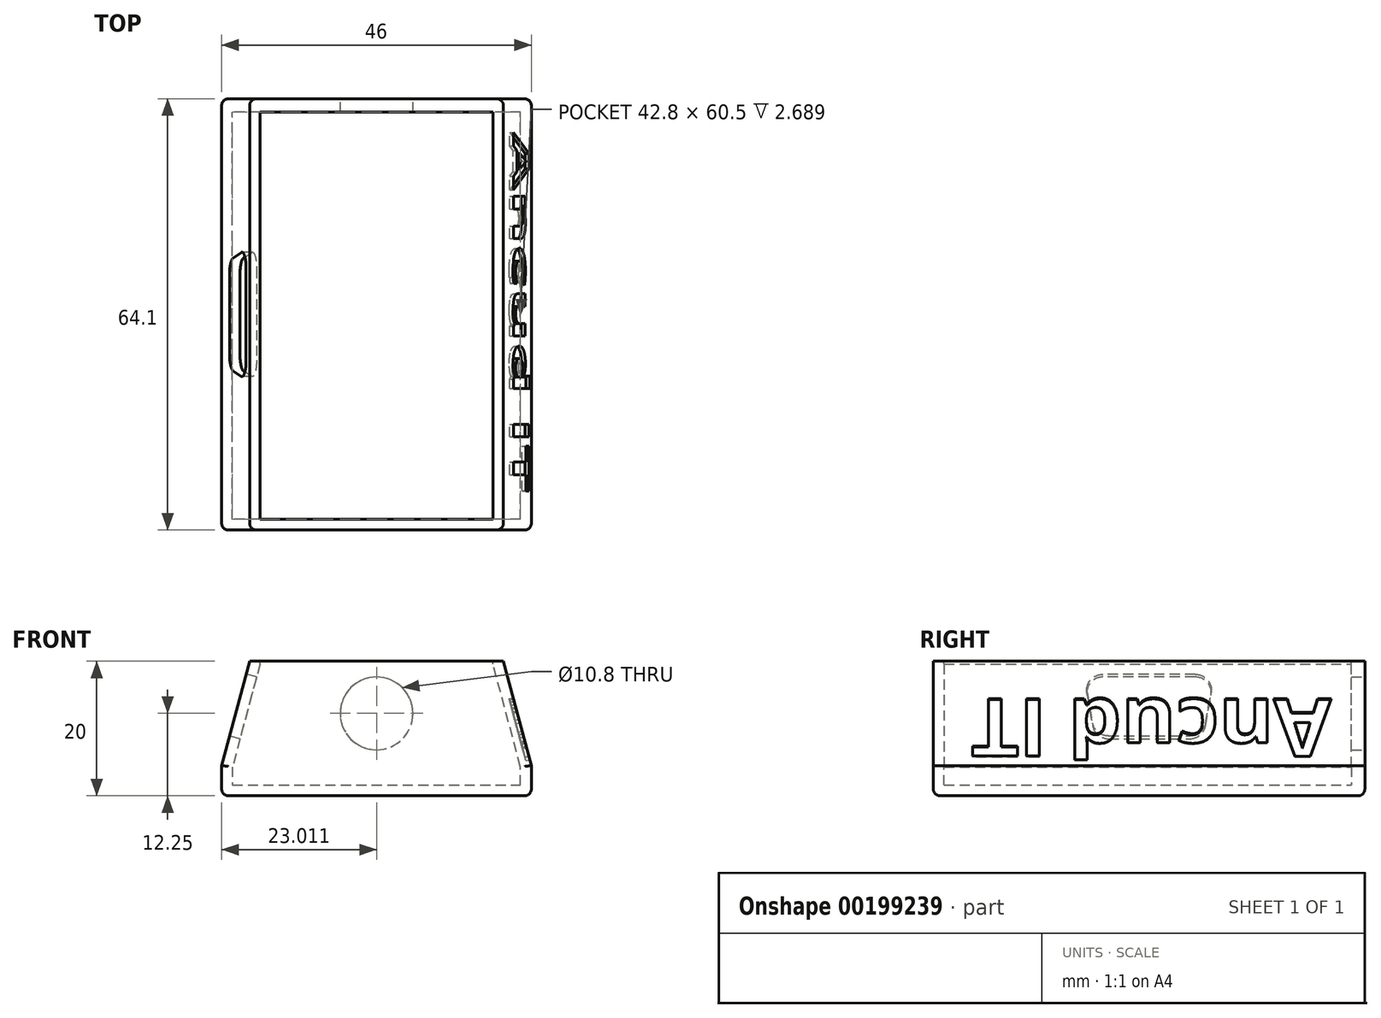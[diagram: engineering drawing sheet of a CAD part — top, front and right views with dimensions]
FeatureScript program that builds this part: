
annotation { "Feature Type Name" : "Feature", "Feature Type Description" : "" }
export const myFeature = defineFeature(function(context is Context, id is Id, definition is map)
    precondition{}
    {
        {
            var Q0;
            Q0=qCreatedBy(makeId("Front.planeOp"),FACE);
            var sketch = newSketch(context, id + "F0", { "sketchPlane" : qUnion([Q0])});
            skLineSegment(sketch, "E0", {"start": v(23, 0) * mm, "end": v(-23, 0) * mm});
            skLineSegment(sketch, "E1", {"start": v(-23, 0) * mm, "end": v(-23, 4.5) * mm});
            skLineSegment(sketch, "E2", {"start": v(-23, 4.5) * mm, "end": v(-18.85, 20) * mm});
            skLineSegment(sketch, "E3", {"start": v(-18.85, 20) * mm, "end": v(18.85, 20) * mm});
            skLineSegment(sketch, "E4", {"start": v(18.85, 20) * mm, "end": v(23, 4.5) * mm});
            skLineSegment(sketch, "E5", {"start": v(23, 4.5) * mm, "end": v(23, 0) * mm});
            skSolve(sketch);
        }
        {
            var Q0;
            Q0 = qSketchRegion(id + "F0", true);
            extrude(context, id + "F1", {"entities" : qUnion([Q0]), "depth" : 2 * mm});
        }
        {
            var Q0;
            Q0=makeQuery(id+"F1.opExtrude","CAP_FACE",FACE,{"disambiguationData":[OSD([sQuery(id+"F0.wireOp",EDGE,"E0"),sQuery(id+"F0.wireOp",EDGE,"E1"),sQuery(id+"F0.wireOp",EDGE,"E2"),sQuery(id+"F0.wireOp",EDGE,"E3"),sQuery(id+"F0.wireOp",EDGE,"E4"),sQuery(id+"F0.wireOp",EDGE,"E5")])],"isStart":false});
            var sketch = newSketch(context, id + "F2", { "sketchPlane" : qUnion([Q0])});
            skLineSegment(sketch, "E6", {"start": v(-23, 0) * mm, "end": v(23, 0) * mm});
            skLineSegment(sketch, "E7", {"start": v(23, 0) * mm, "end": v(23, 4.5) * mm});
            skLineSegment(sketch, "E8", {"start": v(23, 4.5) * mm, "end": v(18.85, 20) * mm});
            skLineSegment(sketch, "E9", {"start": v(-18.85, 20) * mm, "end": v(-23, 4.5) * mm});
            skLineSegment(sketch, "E10", {"start": v(-23, 4.5) * mm, "end": v(-23, 0) * mm});
            skLineSegment(sketch, "E11.0", {"start": v(21.4, 4.29) * mm, "end": v(17.3, 19.59) * mm});
            skLineSegment(sketch, "E11.1", {"start": v(-17.3, 19.59) * mm, "end": v(-21.4, 4.29) * mm});
            skLineSegment(sketch, "E11.2", {"start": v(-21.4, 4.29) * mm, "end": v(-21.4, 1.6) * mm});
            skLineSegment(sketch, "E11.3", {"start": v(-21.4, 1.6) * mm, "end": v(21.4, 1.6) * mm});
            skLineSegment(sketch, "E11.4", {"start": v(21.4, 1.6) * mm, "end": v(21.4, 4.29) * mm});
            skLineSegment(sketch, "E12", {"start": v(-17.3, 19.59) * mm, "end": v(-17.3, 20) * mm});
            skLineSegment(sketch, "E13", {"start": v(17.3, 19.59) * mm, "end": v(17.3, 20) * mm});
            skLineSegment(sketch, "E14", {"start": v(-18.85, 20) * mm, "end": v(-17.3, 20) * mm});
            skLineSegment(sketch, "E15", {"start": v(17.3, 20) * mm, "end": v(18.85, 20) * mm});
            skSolve(sketch);
        }
        {
            var Q0;
            Q0 = qSketchRegion(id + "F2", true);
            extrude(context, id + "F3", {"entities" : qUnion([Q0]), "operationType" : NewBodyOperationType.ADD, "depth" : 60.5 * mm});
        }
        {
            var Q0;
            Q0=makeQuery(id+"F3.opExtrude","CAP_FACE",FACE,{"disambiguationData":[OSD([sQuery(id+"F2.wireOp",EDGE,"E6"),sQuery(id+"F2.wireOp",EDGE,"E7"),sQuery(id+"F2.wireOp",EDGE,"E8"),sQuery(id+"F2.wireOp",EDGE,"E9"),sQuery(id+"F2.wireOp",EDGE,"E10"),sQuery(id+"F2.wireOp",EDGE,"E11.0"),sQuery(id+"F2.wireOp",EDGE,"E11.1"),sQuery(id+"F2.wireOp",EDGE,"E11.2"),sQuery(id+"F2.wireOp",EDGE,"E11.3"),sQuery(id+"F2.wireOp",EDGE,"E11.4"),sQuery(id+"F2.wireOp",EDGE,"E12"),sQuery(id+"F2.wireOp",EDGE,"E13"),sQuery(id+"F2.wireOp",EDGE,"E14"),sQuery(id+"F2.wireOp",EDGE,"E15")])],"isStart":false});
            var sketch = newSketch(context, id + "F4", { "sketchPlane" : qUnion([Q0])});
            skLineSegment(sketch, "E16", {"start": v(-23, 0) * mm, "end": v(23, 0) * mm});
            skLineSegment(sketch, "E17", {"start": v(23, 0) * mm, "end": v(23, 4.5) * mm});
            skLineSegment(sketch, "E18", {"start": v(23, 4.5) * mm, "end": v(18.85, 20) * mm});
            skLineSegment(sketch, "E19", {"start": v(18.85, 20) * mm, "end": v(-18.85, 20) * mm});
            skLineSegment(sketch, "E20", {"start": v(-18.85, 20) * mm, "end": v(-23, 4.5) * mm});
            skLineSegment(sketch, "E21", {"start": v(-23, 4.5) * mm, "end": v(-23, 0) * mm});
            skSolve(sketch);
        }
        {
            var Q0;
            Q0 = qSketchRegion(id + "F4", true);
            extrude(context, id + "F5", {"entities" : qUnion([Q0]), "operationType" : NewBodyOperationType.ADD, "depth" : 1.6 * mm});
        }
        {
            var Q0;
            Q0=makeQuery(id+"F1.opExtrude","CAP_FACE",FACE,{"disambiguationData":[OSD([sQuery(id+"F0.wireOp",EDGE,"E0"),sQuery(id+"F0.wireOp",EDGE,"E1"),sQuery(id+"F0.wireOp",EDGE,"E2"),sQuery(id+"F0.wireOp",EDGE,"E3"),sQuery(id+"F0.wireOp",EDGE,"E4"),sQuery(id+"F0.wireOp",EDGE,"E5")])],"isStart":true});
            var sketch = newSketch(context, id + "F6", { "sketchPlane" : qUnion([Q0])});
            skCircle(sketch, "E22", {"center": v(-0.01, 12.25) * mm, "radius": 5.4 * mm});
            skPoint(sketch, "E22.centerSnap0", {"position": v(-20.92, 12.25) * mm});
            skSolve(sketch);
        }
        {
            var Q0;
            Q0=makeQuery(id+"F5.boolean.opBoolean","MERGE",FACE,{"derivedFrom":[makeQuery(id+"F3.boolean.opBoolean","MERGE",FACE,{"derivedFrom":[makeQuery(id+"F1.opExtrude","SWEPT_FACE",FACE,{"disambiguationData":[OSD([sQuery(id+"F0.wireOp",EDGE,"E2")])]}),makeQuery(id+"F3.opExtrude","SWEPT_FACE",FACE,{"disambiguationData":[OSD([sQuery(id+"F2.wireOp",EDGE,"E9")])]})]}),makeQuery(id+"F5.opExtrude","SWEPT_FACE",FACE,{"disambiguationData":[OSD([sQuery(id+"F4.wireOp",EDGE,"E20")])]})]});
            var sketch = newSketch(context, id + "F7", { "sketchPlane" : qUnion([Q0])});
            skLineSegment(sketch, "E23", {"start": v(25.2, 12.44) * mm, "end": v(38.9, 12.44) * mm});
            skLineSegment(sketch, "E24", {"start": v(41.26, 9.62) * mm, "end": v(40.43, 4.92) * mm});
            skLineSegment(sketch, "E25", {"start": v(38.07, 2.94) * mm, "end": v(26.03, 2.94) * mm});
            skLineSegment(sketch, "E26", {"start": v(23.66, 4.92) * mm, "end": v(22.84, 9.62) * mm});
            skPoint(sketch, "E27.visualSharp", {"position": v(41.76, 12.44) * mm});
            skArc(sketch, "E27.filletArc", {"start": v(41.26, 9.62) * mm, "mid": v(40.74, 11.58) * mm, "end": v(38.9, 12.44) * mm});
            skPoint(sketch, "E28.visualSharp", {"position": v(40.08, 2.94) * mm});
            skArc(sketch, "E28.filletArc", {"start": v(38.07, 2.94) * mm, "mid": v(39.61, 3.5) * mm, "end": v(40.43, 4.92) * mm});
            skPoint(sketch, "E29.visualSharp", {"position": v(24.01, 2.94) * mm});
            skArc(sketch, "E29.filletArc", {"start": v(23.66, 4.92) * mm, "mid": v(24.49, 3.5) * mm, "end": v(26.03, 2.94) * mm});
            skPoint(sketch, "E30.visualSharp", {"position": v(22.34, 12.44) * mm});
            skArc(sketch, "E30.filletArc", {"start": v(25.2, 12.44) * mm, "mid": v(23.36, 11.58) * mm, "end": v(22.84, 9.62) * mm});
            skSolve(sketch);
        }
        {
            var Q0;
            Q0 = qSketchRegion(id + "F6", true);
            extrude(context, id + "F8", {"entities" : qUnion([Q0]), "operationType" : NewBodyOperationType.REMOVE, "endBound" : BoundingType.UP_TO_NEXT, "oppositeDirection" : true, "depth" : 25 * mm});
        }
        {
            var Q0;
            Q0=makeQuery(id+"F1.opExtrude","CAP_EDGE",EDGE,{"disambiguationData":[OSD([sQuery(id+"F0.wireOp",EDGE,"E4")])],"isStart":true});
            var Q1;
            Q1=makeQuery(id+"F1.opExtrude","CAP_EDGE",EDGE,{"disambiguationData":[OSD([sQuery(id+"F0.wireOp",EDGE,"E2")])],"isStart":true});
            var Q2;
            Q2=makeQuery(id+"F5.opExtrude","CAP_EDGE",EDGE,{"disambiguationData":[OSD([sQuery(id+"F4.wireOp",EDGE,"E20")])],"isStart":false});
            var Q3;
            Q3=makeQuery(id+"F5.opExtrude","CAP_EDGE",EDGE,{"disambiguationData":[OSD([sQuery(id+"F4.wireOp",EDGE,"E18")])],"isStart":false});
            var Q4;
            Q4=makeQuery(id+"F5.opExtrude","CAP_EDGE",EDGE,{"disambiguationData":[OSD([sQuery(id+"F4.wireOp",EDGE,"E16")])],"isStart":false});
            var Q5;
            Q5=makeQuery(id+"F5.boolean.opBoolean","MERGE",EDGE,{"derivedFrom":[makeQuery(id+"F3.boolean.opBoolean","MERGE",EDGE,{"derivedFrom":[makeQuery(id+"F1.opExtrude","SWEPT_EDGE",EDGE,{"disambiguationData":[OSD([sQuery(id+"F0.wireOp",EDGE,"E0"),sQuery(id+"F0.wireOp",EDGE,"E1")])]}),makeQuery(id+"F3.opExtrude","SWEPT_EDGE",EDGE,{"disambiguationData":[OSD([sQuery(id+"F2.wireOp",EDGE,"E6"),sQuery(id+"F2.wireOp",EDGE,"E10")])]})]}),makeQuery(id+"F5.opExtrude","SWEPT_EDGE",EDGE,{"disambiguationData":[OSD([sQuery(id+"F4.wireOp",EDGE,"E16"),sQuery(id+"F4.wireOp",EDGE,"E21")])]})]});
            var Q6;
            Q6=makeQuery(id+"F5.boolean.opBoolean","MERGE",EDGE,{"derivedFrom":[makeQuery(id+"F3.boolean.opBoolean","MERGE",EDGE,{"derivedFrom":[makeQuery(id+"F1.opExtrude","SWEPT_EDGE",EDGE,{"disambiguationData":[OSD([sQuery(id+"F0.wireOp",EDGE,"E0"),sQuery(id+"F0.wireOp",EDGE,"E5")])]}),makeQuery(id+"F3.opExtrude","SWEPT_EDGE",EDGE,{"disambiguationData":[OSD([sQuery(id+"F2.wireOp",EDGE,"E6"),sQuery(id+"F2.wireOp",EDGE,"E7")])]})]}),makeQuery(id+"F5.opExtrude","SWEPT_EDGE",EDGE,{"disambiguationData":[OSD([sQuery(id+"F4.wireOp",EDGE,"E16"),sQuery(id+"F4.wireOp",EDGE,"E17")])]})]});
            var Q7;
            Q7=makeQuery(id+"F1.opExtrude","CAP_EDGE",EDGE,{"disambiguationData":[OSD([sQuery(id+"F0.wireOp",EDGE,"E0")])],"isStart":true});
            var Q8;
            Q8=makeQuery(id+"F5.opExtrude","CAP_EDGE",EDGE,{"disambiguationData":[OSD([sQuery(id+"F4.wireOp",EDGE,"E17")])],"isStart":false});
            var Q9;
            Q9=makeQuery(id+"F5.opExtrude","CAP_EDGE",EDGE,{"disambiguationData":[OSD([sQuery(id+"F4.wireOp",EDGE,"E21")])],"isStart":false});
            var Q10;
            Q10=makeQuery(id+"F1.opExtrude","CAP_EDGE",EDGE,{"disambiguationData":[OSD([sQuery(id+"F0.wireOp",EDGE,"E5")])],"isStart":true});
            var Q11;
            Q11=makeQuery(id+"F1.opExtrude","CAP_EDGE",EDGE,{"disambiguationData":[OSD([sQuery(id+"F0.wireOp",EDGE,"E1")])],"isStart":true});
            fillet(context, id + "F9", {"entities" : qUnion([Q0, Q1, Q2, Q3, Q4, Q5, Q6, Q7, Q8, Q9, Q10, Q11]), "radius" : 1 * mm, "tangentPropagation" : true, "allowEdgeOverflow" : false});
        }
        {
            var Q0;
            Q0=makeQuery(id+"F5.boolean.opBoolean","MERGE",FACE,{"derivedFrom":[makeQuery(id+"F3.boolean.opBoolean","MERGE",FACE,{"derivedFrom":[makeQuery(id+"F1.opExtrude","SWEPT_FACE",FACE,{"disambiguationData":[OSD([sQuery(id+"F0.wireOp",EDGE,"E4")])]}),makeQuery(id+"F3.opExtrude","SWEPT_FACE",FACE,{"disambiguationData":[OSD([sQuery(id+"F2.wireOp",EDGE,"E8")])]})]}),makeQuery(id+"F5.opExtrude","SWEPT_FACE",FACE,{"disambiguationData":[OSD([sQuery(id+"F4.wireOp",EDGE,"E18")])]})]});
            var sketch = newSketch(context, id + "F10", { "sketchPlane" : qUnion([Q0])});
            skPoint(sketch, "E31", {"position": v(-32.05, -1.6) * mm});
            skText(sketch, "E32", { "text": "Ancud IT", "fontName": "OpenSans-Bold.ttf"});
            const initialGuessF10  = {"E32": [-0.005, 0.0087, -1, 0, 0.00892]};
            skSetInitialGuess(sketch, initialGuessF10);
            skSolve(sketch);
        }
        {
            var Q0;
            Q0 = qSketchRegion(id + "F10", true);
            var Q1;
            Q1=makeQuery(id+"F3.opExtrude","SWEPT_FACE",FACE,{"disambiguationData":[OSD([sQuery(id+"F2.wireOp",EDGE,"E11.0")])]});
            extrude(context, id + "F11", {"entities" : qUnion([Q0]), "operationType" : NewBodyOperationType.REMOVE, "oppositeDirection" : true, "endBoundEntityFace" : qUnion([Q1]), "depth" : 0.6 * mm});
        }
        {
            var Q0;
            Q0 = qSketchRegion(id + "F7", true);
            extrude(context, id + "F12", {"entities" : qUnion([Q0]), "operationType" : NewBodyOperationType.REMOVE, "endBound" : BoundingType.UP_TO_NEXT, "oppositeDirection" : true, "depth" : 25 * mm});
        }
    });
